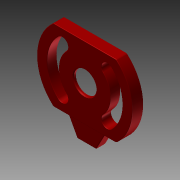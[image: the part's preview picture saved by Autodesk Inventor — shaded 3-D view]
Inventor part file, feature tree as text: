
AUTODESK INVENTOR PART (.ipt)
format: ipt  version: 2013 (Build 170138000, 138)  size: 637,952 bytes
history: native  units: in
note: dims shown in document units (in); Inventor stores cm internally (conversion verified against a paired STEP export)
features: extrude x8, fillet x7, sketch x6, shell x1, chamfer x1
ambient origin geometry x8: Origin, YZ Plane, XZ Plane, XY Plane, X Axis, Y Axis, Z Axis, Center Point
bodies: Solid1 (feature_tree)
feature tree (23):
  sketch  "Sketch1"  dims[d0=0.148in d1=0.0in d2=0.118in d3=0.0in]
  extrude  "Extrusion1"  Depth=0.118in TaperAngle=0.0deg
  extrude  "Extrusion2"  Depth=0.118in TaperAngle=0.0deg
  shell  "Shell1"  Thickness=0.108in
  extrude  "Extrusion3"  Depth=0.039in
  sketch  "Sketch4"  dims[d13=0.012in d18=0.008in]
  extrude  "Extrusion4"  Depth=0.008in
  extrude  "Extrusion9"  Depth=0.108in TaperAngle=0.0deg
  fillet  "Fillet1"  Radius=0.128in
  fillet  "Fillet2"  Radius=0.02in
  fillet  "Fillet3"  Radius=0.189in
  fillet  "Fillet7"  Radius=0.0945in
  fillet  "Fillet8"  Radius=0.012in
  extrude  "Extrusion6"  Depth=0.012in
  chamfer  "Chamfer1"  Distance=0.012in
  extrude  "Extrusion10"  Depth=0.453in
  extrude  "Extrusion12"  Depth=0.354in
  fillet  "Fillet10"  Radius=0.02in
  fillet  "Fillet11"  Radius=0.02in
  sketch  "Sketch2"  dims[d4=0.039in d5=0.118in d6=0.0in d7=0.108in d8=0.0in]
  sketch  "Sketch3"  dims[d11=0.008in d12=0.039in]
  sketch  "Sketch5"  dims[d19=0.016in d20=0.108in d21=0.0in]
  sketch  "Sketch6"  dims[d23=0.012in d24=0.125in d25=45.0deg d30=0.128in d31=0.0in d32=0.02in d33=0.0in d37=0.189in d38=0.0945in d39=0.012in d40=0.012in d41=0.012in d42=0.453in d43=0.354in d44=0.02in d45=0.0in d46=0.02in d47=0.016in d48=0.008in]
